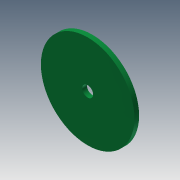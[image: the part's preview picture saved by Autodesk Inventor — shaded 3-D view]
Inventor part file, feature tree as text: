
AUTODESK INVENTOR PART (.ipt)
format: ipt  version: 2013 (Build 170138000, 138)  size: 79,360 bytes
history: native  units: mm
features: extrude x2, sketch x2
ambient origin geometry x8: Origin, YZ Plane, XZ Plane, XY Plane, X Axis, Y Axis, Z Axis, Center Point
bodies: Solid1 (feature_tree)
feature tree (4):
  extrude  "Extrusion1"  Depth=3.0mm TaperAngle=0.0deg
  extrude  "Extrusion2"  Depth=3.0mm TaperAngle=0.0deg
  sketch  "Sketch1"  dims[d0=60.191mm d1=3.0mm d2=0.0mm]
  sketch  "Sketch2"  dims[d3=7.0mm d5=3.0mm d6=0.0mm]
